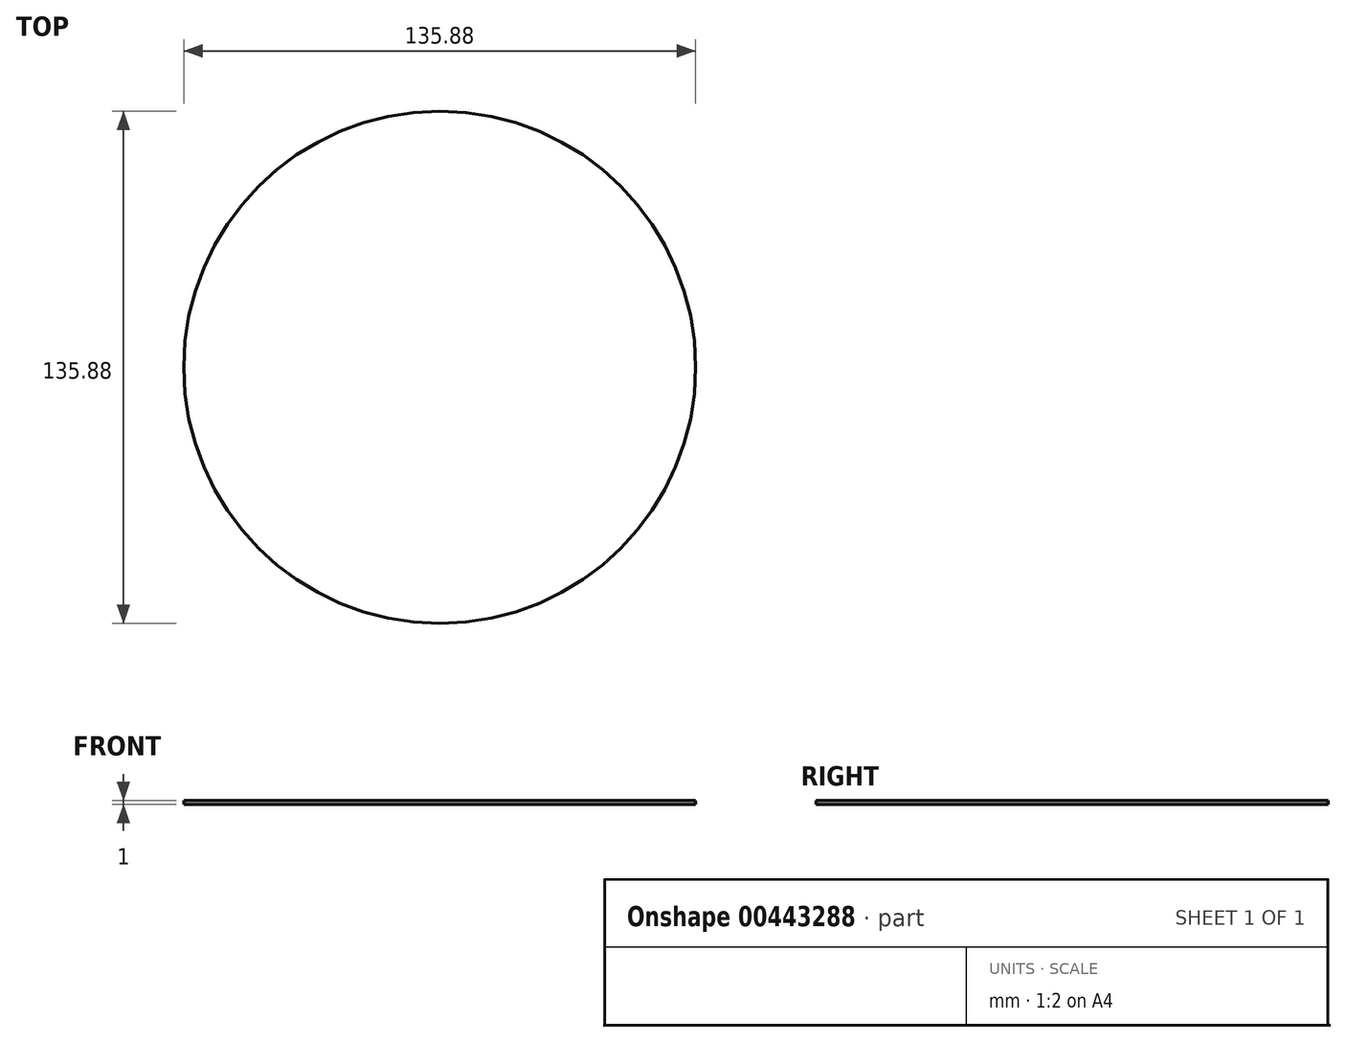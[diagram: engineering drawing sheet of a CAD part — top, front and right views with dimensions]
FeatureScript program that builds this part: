
annotation { "Feature Type Name" : "Feature", "Feature Type Description" : "" }
export const myFeature = defineFeature(function(context is Context, id is Id, definition is map)
    precondition{}
    {
        {
            var Q0;
            Q0=qCreatedBy(makeId("Top.planeOp"),FACE);
            var sketch = newSketch(context, id + "F0", { "sketchPlane" : qUnion([Q0])});
            skCircle(sketch, "E0", {"center": v(0, 0) * mm, "radius": 67.94 * mm});
            skSolve(sketch);
        }
        {
            var Q0;
            Q0 = qSketchRegion(id + "F0", true);
            extrude(context, id + "F1", {"entities" : qUnion([Q0]), "depth" : 1 * mm});
        }
    });
